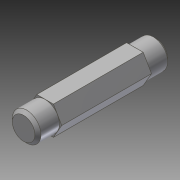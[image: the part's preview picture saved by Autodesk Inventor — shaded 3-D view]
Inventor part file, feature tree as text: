
AUTODESK INVENTOR PART (.ipt)
format: ipt  version: 2014 SP1 (Build 180222100, 222)  size: 85,504 bytes
history: native  units: in
note: dims shown in document units (in); Inventor stores cm internally (conversion verified against a paired STEP export)
features: chamfer x1, other x1, imported_body x1
ambient origin geometry x8: Origin, YZ Plane, XZ Plane, XY Plane, X Axis, Y Axis, Z Axis, Center Point
bodies: Body1 (feature_tree)
feature tree (3):
  chamfer  "Chamfer1"  [1 undecoded]
  other  "217-2428-004 Rev3.ipt1"
  imported_body  "Base1"
note: 1 required parameter value undecoded (feature->parameter linkage not recoverable at this tier; creation-order binding heuristic only, values carry confidence <= 0.55)
